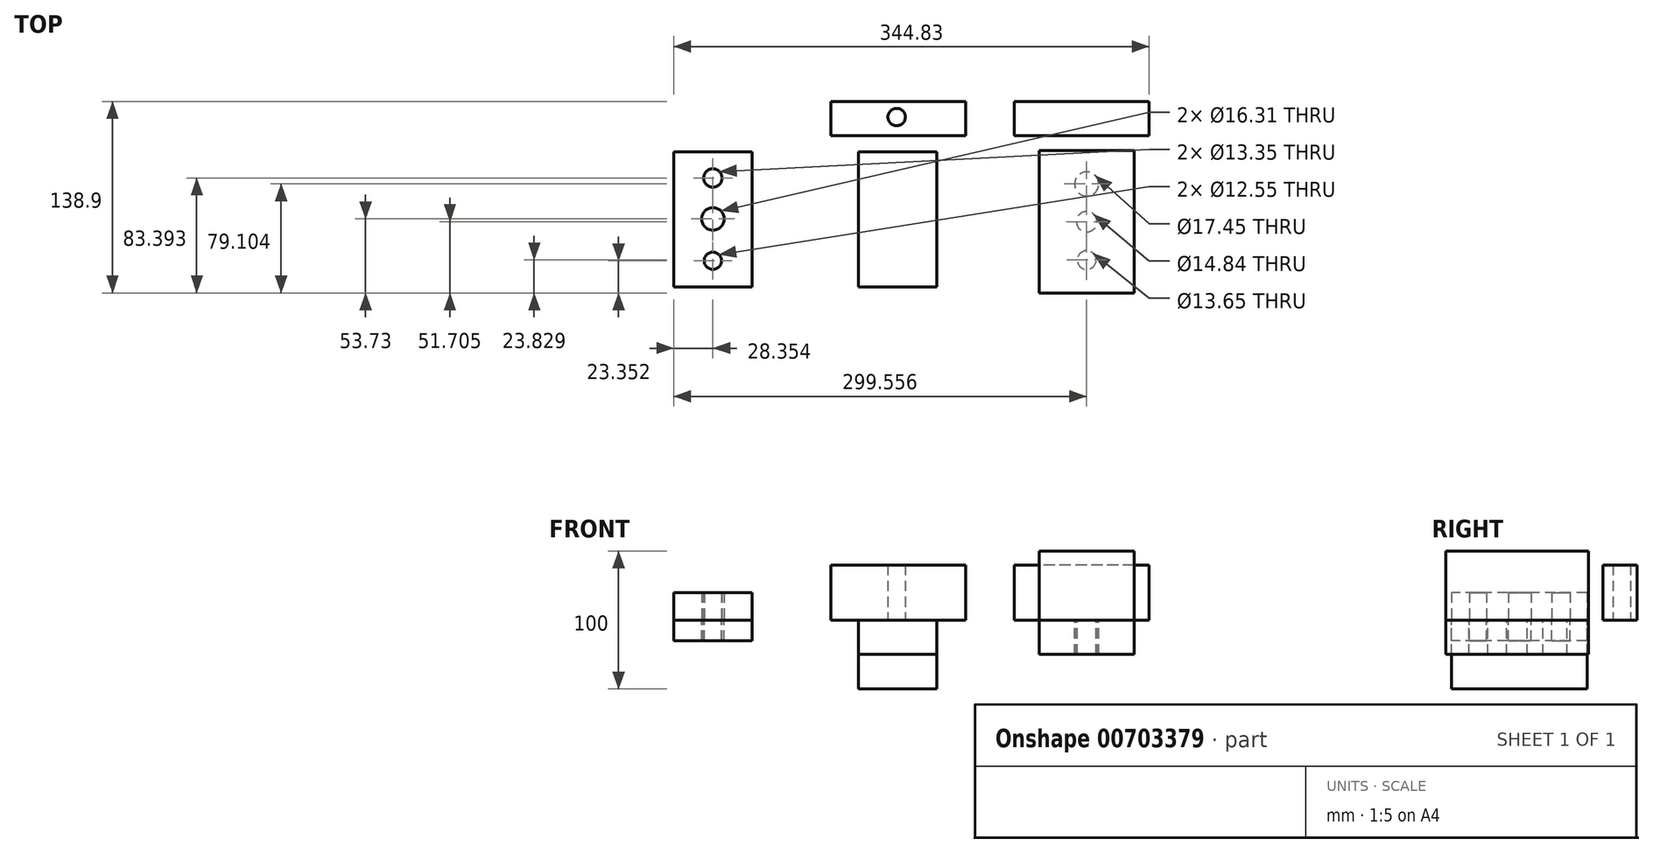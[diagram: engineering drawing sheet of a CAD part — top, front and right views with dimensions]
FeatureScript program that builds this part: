
annotation { "Feature Type Name" : "Feature", "Feature Type Description" : "" }
export const myFeature = defineFeature(function(context is Context, id is Id, definition is map)
    precondition{}
    {
        {
            var Q0;
            Q0=qCreatedBy(makeId("Top.planeOp"),FACE);
            var sketch = newSketch(context, id + "F0", { "sketchPlane" : qUnion([Q0])});
            skLineSegment(sketch, "E0.bottom", {"start": v(-95.42, 48.72) * mm, "end": v(-38.72, 48.72) * mm, "construction": true});
            skLineSegment(sketch, "E0.top", {"start": v(-95.42, -49.44) * mm, "end": v(-38.72, -49.44) * mm, "construction": true});
            skLineSegment(sketch, "E0.left", {"start": v(-95.42, 48.72) * mm, "end": v(-95.42, -49.44) * mm, "construction": true});
            skLineSegment(sketch, "E0.right", {"start": v(-38.72, 48.72) * mm, "end": v(-38.72, -49.44) * mm, "construction": true});
            skLineSegment(sketch, "E1", {"start": v(-67.07, 48.72) * mm, "end": v(-67.07, -49.44) * mm, "construction": true});
            skPoint(sketch, "E2", {"position": v(-67.07, 29.66) * mm});
            skPoint(sketch, "E3", {"position": v(-67.07, 0) * mm});
            skPoint(sketch, "E4", {"position": v(-67.07, -30.38) * mm});
            skCircle(sketch, "E5", {"center": v(-67.07, 29.66) * mm, "radius": 6.68 * mm, "construction": true});
            skCircle(sketch, "E6", {"center": v(-67.07, 0) * mm, "radius": 8.15 * mm, "construction": true});
            skCircle(sketch, "E7", {"center": v(-67.07, -30.38) * mm, "radius": 6.5 * mm, "construction": true});
            skLineSegment(sketch, "E8.bottom", {"start": v(35.62, 49.68) * mm, "end": v(104.71, 49.68) * mm});
            skLineSegment(sketch, "E8.top", {"start": v(35.62, -53.73) * mm, "end": v(104.71, -53.73) * mm});
            skLineSegment(sketch, "E8.left", {"start": v(35.62, 49.68) * mm, "end": v(35.62, -53.73) * mm});
            skLineSegment(sketch, "E8.right", {"start": v(104.71, 49.68) * mm, "end": v(104.71, -53.73) * mm});
            skLineSegment(sketch, "E9", {"start": v(70.17, 49.68) * mm, "end": v(70.17, -53.73) * mm, "construction": true});
            skPoint(sketch, "E10", {"position": v(70.17, 25.37) * mm});
            skPoint(sketch, "E11", {"position": v(70.17, -2.03) * mm});
            skPoint(sketch, "E12", {"position": v(70.17, -29.9) * mm});
            skCircle(sketch, "E13", {"center": v(70.17, 25.37) * mm, "radius": 8.72 * mm});
            skCircle(sketch, "E14", {"center": v(70.17, -2.03) * mm, "radius": 7.42 * mm});
            skCircle(sketch, "E15", {"center": v(70.17, -29.9) * mm, "radius": 6.83 * mm});
            skLineSegment(sketch, "E16.bottom", {"start": v(-115.44, 85.17) * mm, "end": v(-17.61, 85.17) * mm, "construction": true});
            skLineSegment(sketch, "E16.top", {"start": v(-115.44, 60.3) * mm, "end": v(-17.61, 60.3) * mm, "construction": true});
            skLineSegment(sketch, "E16.left", {"start": v(-115.44, 85.17) * mm, "end": v(-115.44, 60.3) * mm, "construction": true});
            skLineSegment(sketch, "E16.right", {"start": v(-17.61, 85.17) * mm, "end": v(-17.61, 60.3) * mm, "construction": true});
            skCircle(sketch, "E17", {"center": v(-67.7, 73.92) * mm, "radius": 6.33 * mm});
            skLineSegment(sketch, "E18.MirrorCS", {"start": v(115.44, 85.17) * mm, "end": v(17.61, 85.17) * mm, "construction": true});
            skLineSegment(sketch, "E19.MirrorCS", {"start": v(115.44, 85.17) * mm, "end": v(115.44, 60.3) * mm, "construction": true});
            skCircle(sketch, "E20.MirrorC", {"center": v(67.7, 73.92) * mm, "radius": 6.33 * mm});
            skLineSegment(sketch, "E21.MirrorCS", {"start": v(115.44, 60.3) * mm, "end": v(17.61, 60.3) * mm, "construction": true});
            skLineSegment(sketch, "E22.MirrorCS", {"start": v(17.61, 85.17) * mm, "end": v(17.61, 60.3) * mm, "construction": true});
            skSolve(sketch);
        }
        {
            var Q0;
            Q0=makeQuery(id+"F0.imprint","IMPRINT",FACE,{"disambiguationData":[TD([[makeQuery(id+"F0.imprint","IMPRINT",EDGE,{"derivedFrom":sQuery(id+"F0.wireOp",EDGE,"E13")}),1.0]])]});
            var Q1;
            Q1=makeQuery(id+"F0.imprint","IMPRINT",FACE,{"disambiguationData":[TD([[makeQuery(id+"F0.imprint","IMPRINT",EDGE,{"derivedFrom":sQuery(id+"F0.wireOp",EDGE,"E14")}),1.0]])]});
            var Q2;
            Q2=makeQuery(id+"F0.imprint","IMPRINT",FACE,{"disambiguationData":[TD([[makeQuery(id+"F0.imprint","IMPRINT",EDGE,{"derivedFrom":sQuery(id+"F0.wireOp",EDGE,"E15")}),1.0]])]});
            var Q3;
            Q3=makeQuery(id+"F0.imprint","IMPRINT",FACE,{"disambiguationData":[TD([[makeQuery(id+"F0.imprint","IMPRINT",EDGE,{"derivedFrom":sQuery(id+"F0.wireOp",EDGE,"E8.bottom")}),-1.0]])]});
            extrude(context, id + "F1", {"entities" : qUnion([Q0, Q1, Q2, Q3]), "depth" : 50 * mm, "offsetDistance" : 25 * mm});
        }
        {
            var Q0;
            Q0=makeQuery(id+"F0.imprint","IMPRINT",FACE,{"disambiguationData":[TD([[makeQuery(id+"F0.imprint","IMPRINT",EDGE,{"derivedFrom":sQuery(id+"F0.wireOp",EDGE,"E8.bottom")}),-1.0]])]});
            extrude(context, id + "F2", {"entities" : qUnion([Q0]), "oppositeDirection" : true, "depth" : 25 * mm, "offsetDistance" : 25 * mm});
        }
        {
            var Q0;
            Q0=qCreatedBy(makeId("Top.planeOp"),FACE);
            var sketch = newSketch(context, id + "F3", { "sketchPlane" : qUnion([Q0])});
            skLineSegment(sketch, "E23.bottom", {"start": v(-95.42, 48.72) * mm, "end": v(-38.72, 48.72) * mm});
            skLineSegment(sketch, "E23.top", {"start": v(-95.42, -49.44) * mm, "end": v(-38.72, -49.44) * mm});
            skLineSegment(sketch, "E23.left", {"start": v(-95.42, 48.72) * mm, "end": v(-95.42, -49.44) * mm});
            skLineSegment(sketch, "E23.right", {"start": v(-38.72, 48.72) * mm, "end": v(-38.72, -49.44) * mm});
            skCircle(sketch, "E24", {"center": v(-67.07, 29.66) * mm, "radius": 6.68 * mm});
            skCircle(sketch, "E25", {"center": v(-67.07, 0) * mm, "radius": 8.15 * mm});
            skCircle(sketch, "E26", {"center": v(-67.07, -30.38) * mm, "radius": 6.27 * mm});
            skLineSegment(sketch, "E27", {"start": v(-134.05, 63.7) * mm, "end": v(-134.05, -67.34) * mm, "construction": true});
            skLineSegment(sketch, "E28.MirrorCS", {"start": v(-172.68, 48.72) * mm, "end": v(-229.39, 48.72) * mm});
            skLineSegment(sketch, "E29.MirrorCS", {"start": v(-172.68, -49.44) * mm, "end": v(-229.39, -49.44) * mm});
            skLineSegment(sketch, "E30.MirrorCS", {"start": v(-172.68, 48.72) * mm, "end": v(-172.68, -49.44) * mm});
            skLineSegment(sketch, "E31.MirrorCS", {"start": v(-229.39, 48.72) * mm, "end": v(-229.39, -49.44) * mm});
            skCircle(sketch, "E32.MirrorC", {"center": v(-201.04, 29.66) * mm, "radius": 6.68 * mm});
            skCircle(sketch, "E33.MirrorC", {"center": v(-201.04, 0) * mm, "radius": 8.15 * mm});
            skCircle(sketch, "E34.MirrorC", {"center": v(-201.04, -30.38) * mm, "radius": 6.27 * mm});
            skLineSegment(sketch, "E35.bottom", {"start": v(-115.44, 60.37) * mm, "end": v(-17.61, 60.37) * mm});
            skLineSegment(sketch, "E35.top", {"start": v(-115.44, 85.17) * mm, "end": v(-17.61, 85.17) * mm});
            skLineSegment(sketch, "E35.left", {"start": v(-115.44, 60.37) * mm, "end": v(-115.44, 85.17) * mm});
            skLineSegment(sketch, "E35.right", {"start": v(-17.61, 60.37) * mm, "end": v(-17.61, 85.17) * mm});
            skLineSegment(sketch, "E36.MirrorCS", {"start": v(115.44, 60.37) * mm, "end": v(17.61, 60.37) * mm});
            skLineSegment(sketch, "E37.MirrorCS", {"start": v(115.44, 85.17) * mm, "end": v(17.61, 85.17) * mm});
            skLineSegment(sketch, "E38.MirrorCS", {"start": v(115.44, 60.37) * mm, "end": v(115.44, 85.17) * mm});
            skLineSegment(sketch, "E39.MirrorCS", {"start": v(17.61, 60.37) * mm, "end": v(17.61, 85.17) * mm});
            skSolve(sketch);
        }
        {
            var Q0;
            Q0=makeQuery(id+"F3.imprint","IMPRINT",FACE,{"disambiguationData":[TD([[makeQuery(id+"F3.imprint","IMPRINT",EDGE,{"derivedFrom":sQuery(id+"F3.wireOp",EDGE,"E24")}),1.0]])]});
            var Q1;
            Q1=makeQuery(id+"F3.imprint","IMPRINT",FACE,{"disambiguationData":[TD([[makeQuery(id+"F3.imprint","IMPRINT",EDGE,{"derivedFrom":sQuery(id+"F3.wireOp",EDGE,"E25")}),1.0]])]});
            var Q2;
            Q2=makeQuery(id+"F3.imprint","IMPRINT",FACE,{"disambiguationData":[TD([[makeQuery(id+"F3.imprint","IMPRINT",EDGE,{"derivedFrom":sQuery(id+"F3.wireOp",EDGE,"E26")}),1.0]])]});
            var Q3;
            Q3=makeQuery(id+"F3.imprint","IMPRINT",FACE,{"disambiguationData":[TD([[makeQuery(id+"F3.imprint","IMPRINT",EDGE,{"derivedFrom":sQuery(id+"F3.wireOp",EDGE,"E23.bottom")}),-1.0]])]});
            extrude(context, id + "F4", {"entities" : qUnion([Q0, Q1, Q2, Q3]), "oppositeDirection" : true, "depth" : 25 * mm, "offsetDistance" : 25 * mm});
        }
        {
            var Q0;
            Q0=makeQuery(id+"F4.opExtrude","CAP_FACE",FACE,{"disambiguationData":[OSD([sQuery(id+"F3.wireOp",EDGE,"E23.bottom"),sQuery(id+"F3.wireOp",EDGE,"E23.top"),sQuery(id+"F3.wireOp",EDGE,"E23.left"),sQuery(id+"F3.wireOp",EDGE,"E23.right")])],"isStart":false});
            extrude(context, id + "F5", {"entities" : qUnion([Q0]), "depth" : 25 * mm, "offsetDistance" : 25 * mm});
        }
        {
            var Q0;
            Q0=makeQuery(id+"F3.imprint","IMPRINT",FACE,{"disambiguationData":[TD([[makeQuery(id+"F3.imprint","IMPRINT",EDGE,{"derivedFrom":sQuery(id+"F3.wireOp",EDGE,"E28.MirrorCS")}),1.0]])]});
            extrude(context, id + "F6", {"entities" : qUnion([Q0]), "oppositeDirection" : true, "depth" : 15 * mm, "offsetDistance" : 25 * mm});
        }
        {
            var Q0;
            Q0=makeQuery(id+"F3.imprint","IMPRINT",FACE,{"disambiguationData":[TD([[makeQuery(id+"F3.imprint","IMPRINT",EDGE,{"derivedFrom":sQuery(id+"F3.wireOp",EDGE,"E28.MirrorCS")}),1.0]])]});
            extrude(context, id + "F7", {"entities" : qUnion([Q0]), "depth" : 20 * mm, "offsetDistance" : 25 * mm});
        }
        {
            var Q0;
            Q0=makeQuery(id+"F3.imprint","IMPRINT",FACE,{"disambiguationData":[TD([[makeQuery(id+"F3.imprint","IMPRINT",EDGE,{"derivedFrom":sQuery(id+"F3.wireOp",EDGE,"E35.bottom")}),1.0]])]});
            var Q1;
            Q1=makeQuery(id+"F0.imprint","IMPRINT",FACE,{"disambiguationData":[TD([[makeQuery(id+"F0.imprint","IMPRINT",EDGE,{"derivedFrom":sQuery(id+"F0.wireOp",EDGE,"E17")}),1.0]])]});
            extrude(context, id + "F8", {"entities" : qUnion([Q0, Q1]), "depth" : 40 * mm, "offsetDistance" : 25 * mm});
        }
        {
            var Q0;
            Q0=makeQuery(id+"F3.imprint","IMPRINT",FACE,{"disambiguationData":[TD([[makeQuery(id+"F3.imprint","IMPRINT",EDGE,{"derivedFrom":sQuery(id+"F3.wireOp",EDGE,"E36.MirrorCS")}),-1.0]])]});
            extrude(context, id + "F9", {"entities" : qUnion([Q0]), "depth" : 40 * mm, "offsetDistance" : 25 * mm});
        }
    });
